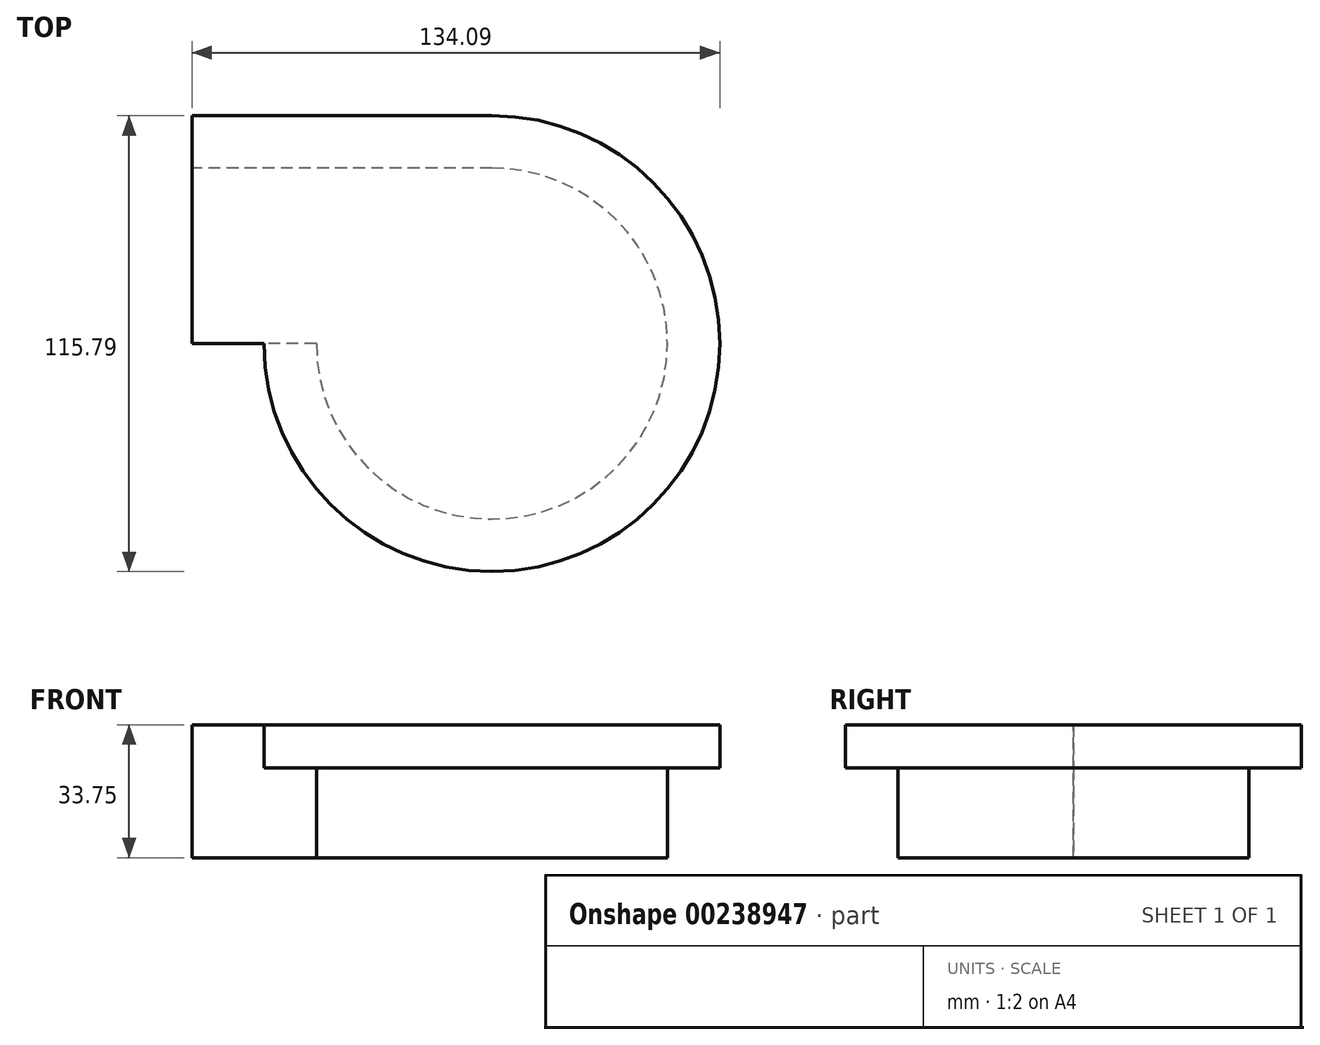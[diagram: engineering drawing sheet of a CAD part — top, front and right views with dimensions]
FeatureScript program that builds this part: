
annotation { "Feature Type Name" : "Feature", "Feature Type Description" : "" }
export const myFeature = defineFeature(function(context is Context, id is Id, definition is map)
    precondition{}
    {
        {
            var Q0;
            Q0=qCreatedBy(makeId("Right.planeOp"),FACE);
            var sketch = newSketch(context, id + "F0", { "sketchPlane" : qUnion([Q0])});
            skLineSegment(sketch, "E0", {"start": v(0, 0) * mm, "end": v(-44.58, 0) * mm});
            skLineSegment(sketch, "E1", {"start": v(-44.58, 0) * mm, "end": v(-44.58, 33.75) * mm});
            skLineSegment(sketch, "E2", {"start": v(-44.58, 33.75) * mm, "end": v(13.3, 33.75) * mm});
            skLineSegment(sketch, "E3", {"start": v(13.3, 33.75) * mm, "end": v(13.3, 22.84) * mm});
            skLineSegment(sketch, "E4", {"start": v(13.3, 22.84) * mm, "end": v(0, 22.84) * mm});
            skLineSegment(sketch, "E5", {"start": v(0, 22.84) * mm, "end": v(0, 0) * mm});
            skSolve(sketch);
        }
        {
            var Q0;
            Q0=makeQuery(id+"F0.imprint","IMPRINT",FACE,{"disambiguationData":[TD([[makeQuery(id+"F0.imprint","IMPRINT",EDGE,{"derivedFrom":sQuery(id+"F0.wireOp",EDGE,"E0")}),-1.0]])]});
            extrude(context, id + "F1", {"entities" : qUnion([Q0]), "depth" : 76.2 * mm});
        }
        {
            var Q0;
            Q0=makeQuery(id+"F1.opExtrude","CAP_FACE",FACE,{"disambiguationData":[OSD([sQuery(id+"F0.wireOp",EDGE,"E0"),sQuery(id+"F0.wireOp",EDGE,"E1"),sQuery(id+"F0.wireOp",EDGE,"E2"),sQuery(id+"F0.wireOp",EDGE,"E3"),sQuery(id+"F0.wireOp",EDGE,"E4"),sQuery(id+"F0.wireOp",EDGE,"E5")])],"isStart":false});
            var Q1;
            Q1=makeQuery(id+"F1.opExtrude","CAP_EDGE",EDGE,{"disambiguationData":[OSD([sQuery(id+"F0.wireOp",EDGE,"E1")])],"isStart":false});
            revolve(context, id + "F2", {"operationType" : NewBodyOperationType.ADD, "entities" : qUnion([Q0]), "axis" : qUnion([Q1]), "revolveType" : RevolveType.FULL});
        }
    });
